# Revit family: Gira_260566
name_source: partatom
category: Electrical Fixtures
revit_build: Autodesk Revit 2017 (Build: 20160225_1515(x64)
units: mm (PartAtom-declared; Revit-internal decimal feet)

## family parameters
Cut with Voids When Loaded = No
Host = Face
Maintain Annotation Orientation = Yes
Part Type = Normal
Room Calculation Point = No
Round Connector Dimension = Use Diameter
Shared = No

## types (1)
- Gira Keyless In Codetastatur Gira TX_44 (WG UP) Reinweiß
    Andere Bussysteme = sonstige
    Anschlussart = Steckklemme
    Anzahl der Betätigungswippen = 2
    Anzahl der Module (bei Modulbauweise) = 1
    Ausführung = Codeschloss
    Ausführung der Oberfläche = nicht zutreffend
    Available = Yes
    BIM (1) = https://media.live.bim.site und Tasten.rfa?public/gira/9fde4c0/TX44_Komplettgerät_Schalten und Tasten.rfa
    Bedienungsart = Wippe/Taste
    Befestigungsart = Krallen-/Schraubbefestigung
    Beleuchtung = nein
    Bemessungsstrom = 10 Ampere
    Bussystem Funkbus = Nein
    Bussystem KNX = Nein
    Bussystem KNX-Funk = Ja
    Bussystem LON = Nein
    Bussystem Powernet = Nein
    Category = Bussystem-Zutrittskontrolleinrichtung
    Data sheet (1) = https://katalog.gira.de
    Default Elevation = 1219 mm
    Description = Tastschalter 10 AX 250 V~ mit Wippe 2fach Serienschalter Reinweiß Hinweise : - Mit abtastbarer Bedienerführung. - Diebstahlschutz durch optional verschraubbares Klemmstück. Dadurch entfällt das Verdübeln der Abdeckrahmen.
    Farbe = weiß
    GTIN = 4010337051428
    Geeignet für Schutzart (IP) = IP44
    HAN = 260566
    Halogenfrei = Ja
    HeinzeBIM = https://bimportal.heinze.de
    Kategorie = Bussystem-Zutrittskontrolleinrichtung
    Keynote = TX44_Komplettgerät_Schalten und Tasten
    Manufacturer = Gira
    Manufacturer URL = https://www.gira.de
    Mit Busankopplung = Ja
    Mit Montageplatte = Nein
    Montageart = unter Putz
    Name = Gira Keyless In Codetastatur Gira TX_44 (WG UP) Reinweiß
    Nennspannung = 250 Volt
    Oberfläche = sonstige
    Region = DE
    Rückmeldekontakt = Nein
    Schaltungsart = Serienschalter
    Schutzart (IP) = IP44
    Tastschalter = Ja
    Textfeld/Beschriftungsfläche = nein
    Transparent = Nein
    URL = http://katalog.gira.de
    Verfügbar = Ja
    Waschmaschinenschalter = Nein
    Werkstoff = sonstige
    Werkstoffgüte = sonstige
    Zusammenstellung = Basiselement mit zentraler Abdeckplatte

## geometry (parser evidence)
native form markers: Blend x2, Sweep x3
no freeform markers — native parametric forms only
